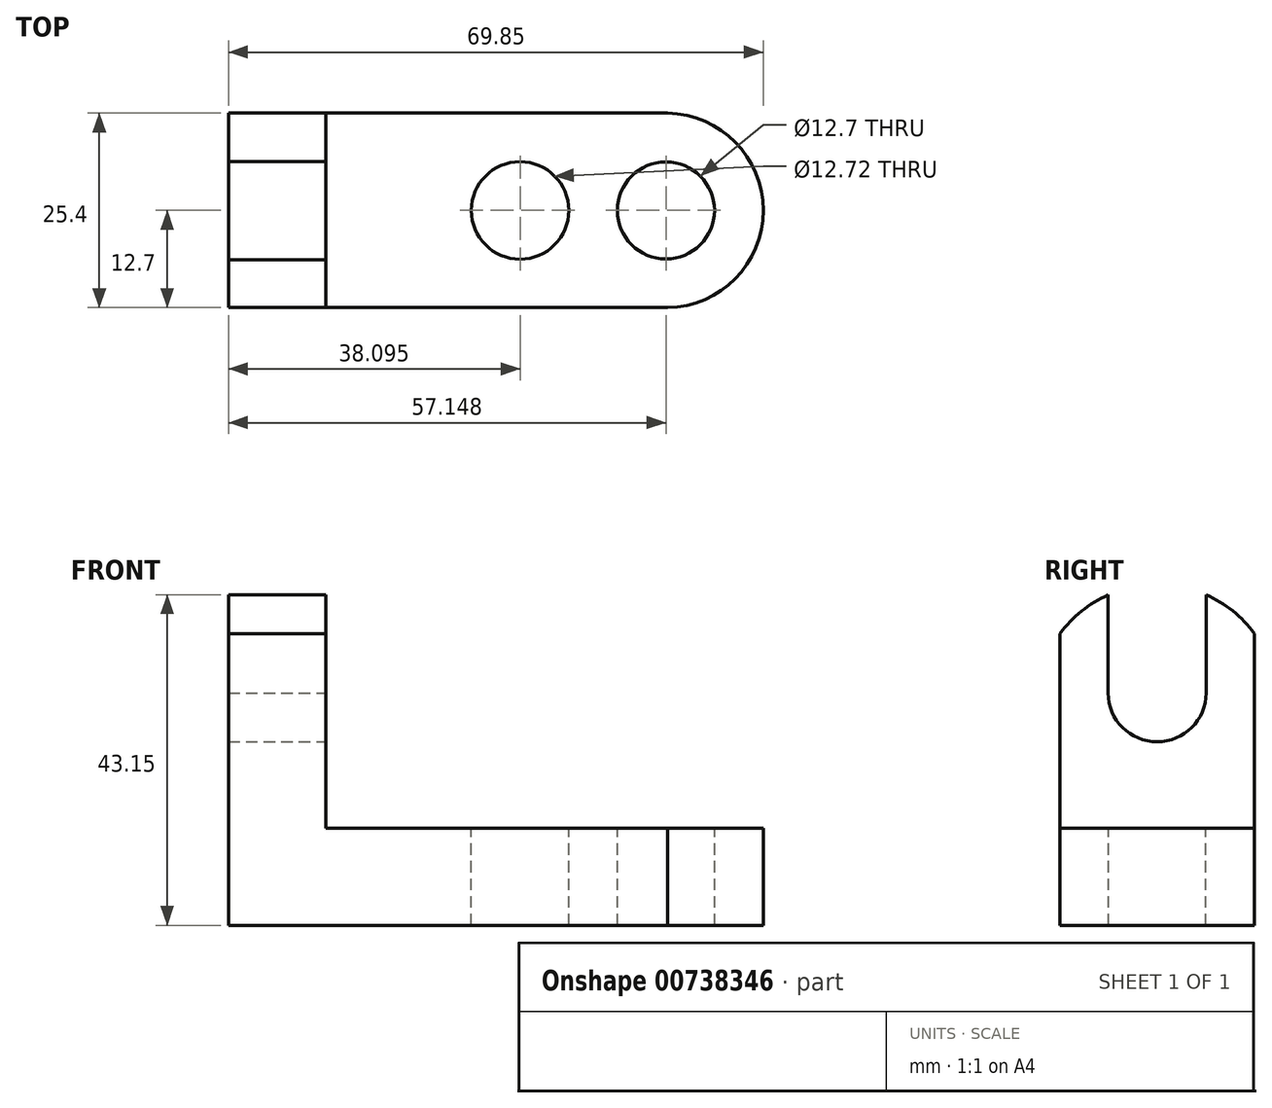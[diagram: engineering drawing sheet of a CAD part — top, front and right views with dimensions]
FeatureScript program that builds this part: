
annotation { "Feature Type Name" : "Feature", "Feature Type Description" : "" }
export const myFeature = defineFeature(function(context is Context, id is Id, definition is map)
    precondition{}
    {
        {
            var Q0;
            Q0=qCreatedBy(makeId("Front.planeOp"),FACE);
            var sketch = newSketch(context, id + "F0", { "sketchPlane" : qUnion([Q0])});
            skLineSegment(sketch, "E0", {"start": v(0, 0) * mm, "end": v(0, 44.45) * mm});
            skLineSegment(sketch, "E1", {"start": v(0, 44.45) * mm, "end": v(12.7, 44.45) * mm});
            skLineSegment(sketch, "E2", {"start": v(12.7, 44.45) * mm, "end": v(12.7, 12.7) * mm});
            skLineSegment(sketch, "E3", {"start": v(12.7, 12.7) * mm, "end": v(69.85, 12.7) * mm});
            skLineSegment(sketch, "E4", {"start": v(69.85, 12.7) * mm, "end": v(69.85, 0) * mm});
            skLineSegment(sketch, "E5", {"start": v(69.85, 0) * mm, "end": v(0, 0) * mm});
            skSolve(sketch);
        }
        {
            var Q0;
            Q0 = qSketchRegion(id + "F0", true);
            extrude(context, id + "F1", {"entities" : qUnion([Q0]), "depth" : 25.4 * mm, "offsetDistance" : 25.4 * mm});
        }
        {
            var Q0;
            Q0=makeQuery(id+"F1.opExtrude","SWEPT_FACE",FACE,{"disambiguationData":[OSD([sQuery(id+"F0.wireOp",EDGE,"E2")])]});
            var sketch = newSketch(context, id + "F2", { "sketchPlane" : qUnion([Q0])});
            skLineSegment(sketch, "E6", {"start": v(-25.4, 38.1) * mm, "end": v(0, 38.1) * mm});
            skLineSegment(sketch, "E7", {"start": v(0, 38.1) * mm, "end": v(0, 44.45) * mm});
            skArc(sketch, "E8", {"start": v(0, 38.1) * mm, "mid": v(-12.7, 44.5) * mm, "end": v(-25.4, 38.1) * mm});
            skSolve(sketch);
        }
        {
            var Q0;
            {var subQ0=sQuery(id+"F2.wireOp",EDGE,"E8");var subQ1=makeQuery(id+"F1.opExtrude","SWEPT_EDGE",EDGE,{"disambiguationData":[OSD([sQuery(id+"F0.wireOp",EDGE,"E1"),sQuery(id+"F0.wireOp",EDGE,"E2")])]});var subQ2=makeQuery(id+"F2.imprint","INTERSECT",VERTEX,{"disambiguationData":[OD(0.0)],"derivedFrom":[subQ1,subQ0]});Q0=makeQuery(id+"F2.imprint","IMPRINT",FACE,{"disambiguationData":[TD([[makeQuery(id+"F2.imprint","IMPRINT",EDGE,{"disambiguationData":[TD([[subQ2,-1.0]])],"derivedFrom":subQ0}),1.0]])]});}
            var Q1;
            {var subQ0=sQuery(id+"F2.wireOp",EDGE,"E8");var subQ1=sQuery(id+"F0.wireOp",EDGE,"E2");var subQ2=makeQuery(id+"F1.opExtrude","CAP_EDGE",EDGE,{"disambiguationData":[OSD([subQ1])],"isStart":false});var subQ3=makeQuery(id+"F2.imprint","INTERSECT",VERTEX,{"derivedFrom":[subQ2,sQuery(id+"F2.wireOp",EDGE,"E6"),subQ0]});Q1=makeQuery(id+"F2.imprint","IMPRINT",FACE,{"disambiguationData":[TD([[makeQuery(id+"F2.imprint","IMPRINT",EDGE,{"disambiguationData":[TD([[subQ3,1.0]])],"derivedFrom":subQ0}),-1.0]])]});}
            var Q2;
            {var subQ0=sQuery(id+"F2.wireOp",EDGE,"E7");Q2=makeQuery(id+"F2.imprint","IMPRINT",FACE,{"disambiguationData":[TD([[makeQuery(id+"F2.imprint","IMPRINT",EDGE,{"derivedFrom":subQ0}),-1.0]])]});}
            extrude(context, id + "F3", {"entities" : qUnion([Q0, Q1, Q2]), "operationType" : NewBodyOperationType.REMOVE, "endBound" : BoundingType.THROUGH_ALL, "oppositeDirection" : true, "depth" : 25.4 * mm, "offsetDistance" : 25.4 * mm});
        }
        {
            var Q0;
            Q0=makeQuery(id+"F1.opExtrude","SWEPT_FACE",FACE,{"disambiguationData":[OSD([sQuery(id+"F0.wireOp",EDGE,"E2")])]});
            var sketch = newSketch(context, id + "F4", { "sketchPlane" : qUnion([Q0])});
            skLineSegment(sketch, "E9", {"start": v(-12.7, 44.45) * mm, "end": v(-12.7, 25.4) * mm});
            skLineSegment(sketch, "E10", {"start": v(-12.7, 25.4) * mm, "end": v(0, 25.4) * mm});
            skLineSegment(sketch, "E11", {"start": v(-19.12, 43.14) * mm, "end": v(-19.12, 30.35) * mm});
            skLineSegment(sketch, "E12", {"start": v(-19.12, 30.35) * mm, "end": v(-6.32, 30.35) * mm});
            skLineSegment(sketch, "E13", {"start": v(-6.32, 30.35) * mm, "end": v(-6.32, 43.15) * mm});
            skCircle(sketch, "E14", {"center": v(-12.72, 30.35) * mm, "radius": 6.4 * mm});
            skSolve(sketch);
        }
        {
            var Q0;
            Q0 = qSketchRegion(id + "F4", true);
            var Q1;
            {var subQ5=sQuery(id+"F4.wireOp",EDGE,"E11");Q1=makeQuery(id+"F4.imprint","IMPRINT",FACE,{"disambiguationData":[TD([[makeQuery(id+"F4.imprint","IMPRINT",EDGE,{"derivedFrom":subQ5}),1.0]])]});}
            var Q2;
            {var subQ9=sQuery(id+"F4.wireOp",EDGE,"E13");Q2=makeQuery(id+"F4.imprint","IMPRINT",FACE,{"disambiguationData":[TD([[makeQuery(id+"F4.imprint","IMPRINT",EDGE,{"derivedFrom":subQ9}),1.0]])]});}
            extrude(context, id + "F5", {"entities" : qUnion([Q0, Q1, Q2]), "operationType" : NewBodyOperationType.REMOVE, "endBound" : BoundingType.THROUGH_ALL, "oppositeDirection" : true, "depth" : 25.4 * mm, "offsetDistance" : 25.4 * mm});
        }
        {
            var Q0;
            Q0=makeQuery(id+"F1.opExtrude","SWEPT_FACE",FACE,{"disambiguationData":[OSD([sQuery(id+"F0.wireOp",EDGE,"E3")])]});
            var sketch = newSketch(context, id + "F6", { "sketchPlane" : qUnion([Q0])});
            skLineSegment(sketch, "E15", {"start": v(56.94, 0) * mm, "end": v(56.94, -25.4) * mm});
            skArc(sketch, "E16", {"start": v(56.94, -25.4) * mm, "mid": v(69.85, -12.7) * mm, "end": v(56.94, 0) * mm});
            skCircle(sketch, "E17", {"center": v(57.15, -12.7) * mm, "radius": 6.35 * mm});
            skLineSegment(sketch, "E18", {"start": v(57.15, -12.7) * mm, "end": v(50.8, -12.7) * mm});
            skLineSegment(sketch, "E19", {"start": v(50.8, -12.7) * mm, "end": v(38.1, -12.7) * mm});
            skCircle(sketch, "E20", {"center": v(38.1, -12.7) * mm, "radius": 6.36 * mm});
            skSolve(sketch);
        }
        {
            var Q0;
            Q0=makeQuery(id+"F6.imprint","IMPRINT",FACE,{"disambiguationData":[TD([[makeQuery(id+"F6.imprint","IMPRINT",EDGE,{"derivedFrom":sQuery(id+"F6.wireOp",EDGE,"E20")}),1.0]])]});
            var Q1;
            {var subQ0=sQuery(id+"F6.wireOp",EDGE,"E18");var subQ1=sQuery(id+"F6.wireOp",EDGE,"E15");var subQ2=makeQuery(id+"F6.imprint","INTERSECT",VERTEX,{"derivedFrom":[subQ1,subQ0]});Q1=makeQuery(id+"F6.imprint","IMPRINT",FACE,{"disambiguationData":[TD([[makeQuery(id+"F6.imprint","IMPRINT",EDGE,{"disambiguationData":[TD([[subQ2,1.0]])],"derivedFrom":subQ1}),-1.0]])]});}
            var Q2;
            {var subQ0=sQuery(id+"F6.wireOp",EDGE,"E18");var subQ1=sQuery(id+"F6.wireOp",EDGE,"E15");var subQ2=makeQuery(id+"F6.imprint","INTERSECT",VERTEX,{"derivedFrom":[subQ1,subQ0]});Q2=makeQuery(id+"F6.imprint","IMPRINT",FACE,{"disambiguationData":[TD([[makeQuery(id+"F6.imprint","IMPRINT",EDGE,{"disambiguationData":[TD([[subQ2,-1.0]])],"derivedFrom":subQ1}),-1.0]])]});}
            var Q3;
            {var subQ0=sQuery(id+"F6.wireOp",EDGE,"E16");var subQ1=makeQuery(id+"F1.opExtrude","CAP_EDGE",EDGE,{"disambiguationData":[OSD([sQuery(id+"F0.wireOp",EDGE,"E3")])],"isStart":false});var subQ3=makeQuery(id+"F6.imprint","INTERSECT",VERTEX,{"derivedFrom":[subQ1,subQ0]});Q3=makeQuery(id+"F6.imprint","IMPRINT",FACE,{"disambiguationData":[TD([[makeQuery(id+"F6.imprint","IMPRINT",EDGE,{"disambiguationData":[TD([[subQ3,1.0]])],"derivedFrom":subQ0}),1.0]])]});}
            var Q4;
            {var subQ0=sQuery(id+"F6.wireOp",EDGE,"E16");var subQ1=makeQuery(id+"F1.opExtrude","CAP_EDGE",EDGE,{"disambiguationData":[OSD([sQuery(id+"F0.wireOp",EDGE,"E3")])],"isStart":true});var subQ3=makeQuery(id+"F6.imprint","INTERSECT",VERTEX,{"derivedFrom":[subQ1,subQ0]});Q4=makeQuery(id+"F6.imprint","IMPRINT",FACE,{"disambiguationData":[TD([[makeQuery(id+"F6.imprint","IMPRINT",EDGE,{"disambiguationData":[TD([[subQ3,-1.0]])],"derivedFrom":subQ0}),1.0]])]});}
            var Q5;
            {var subQ0=sQuery(id+"F6.wireOp",EDGE,"E15");var subQ1=makeQuery(id+"F6.imprint","INTERSECT",VERTEX,{"derivedFrom":[subQ0,sQuery(id+"F6.wireOp",EDGE,"E18")]});Q5=makeQuery(id+"F6.imprint","IMPRINT",FACE,{"disambiguationData":[TD([[makeQuery(id+"F6.imprint","IMPRINT",EDGE,{"disambiguationData":[TD([[subQ1,1.0]])],"derivedFrom":subQ0}),1.0]])]});}
            var Q6;
            {var subQ1=sQuery(id+"F0.wireOp",EDGE,"E3");var subQ6=makeQuery(id+"F1.opExtrude","SWEPT_EDGE",EDGE,{"disambiguationData":[OSD([subQ1,sQuery(id+"F0.wireOp",EDGE,"E4")])]});Q6=makeQuery(id+"F6.imprint","IMPRINT",FACE,{"disambiguationData":[TD([[makeQuery(id+"F6.imprint","IMPRINT",EDGE,{"derivedFrom":subQ6}),1.0]])]});}
            extrude(context, id + "F7", {"entities" : qUnion([Q0, Q1, Q2, Q3, Q4, Q5, Q6]), "operationType" : NewBodyOperationType.REMOVE, "endBound" : BoundingType.THROUGH_ALL, "oppositeDirection" : true, "depth" : 25.4 * mm, "offsetDistance" : 25.4 * mm});
        }
    });
